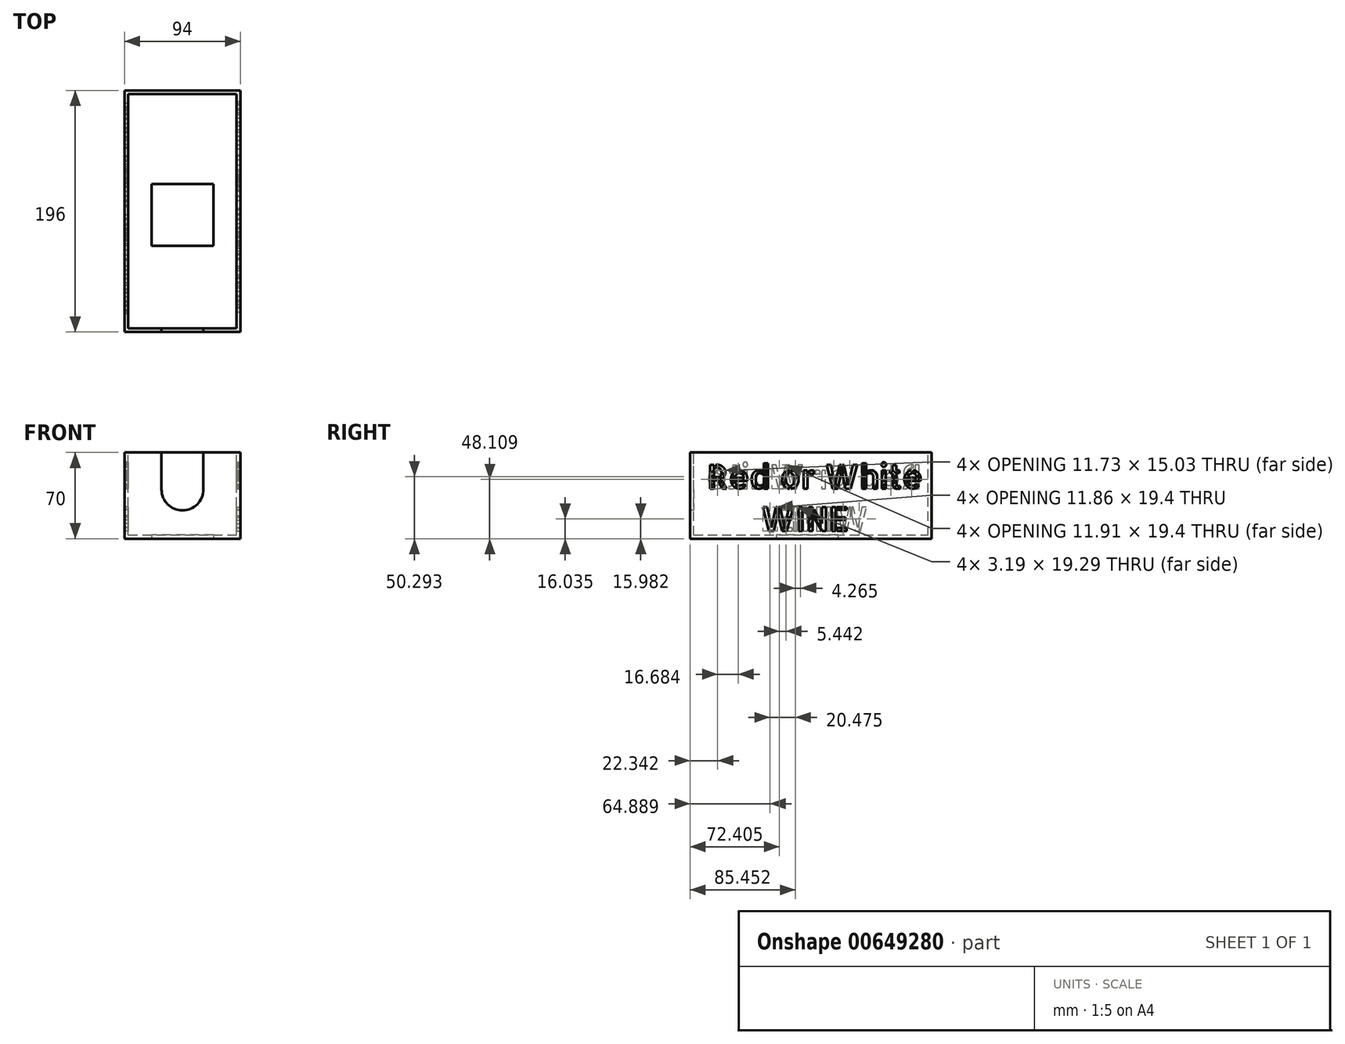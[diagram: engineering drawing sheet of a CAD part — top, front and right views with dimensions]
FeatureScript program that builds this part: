
annotation { "Feature Type Name" : "Feature", "Feature Type Description" : "" }
export const myFeature = defineFeature(function(context is Context, id is Id, definition is map)
    precondition{}
    {
        {
            var Q0;
            Q0=qCreatedBy(makeId("Front.planeOp"),FACE);
            var sketch = newSketch(context, id + "F0", { "sketchPlane" : qUnion([Q0])});
            skLineSegment(sketch, "E0.bottom", {"start": v(-47, 0) * mm, "end": v(47, 0) * mm});
            skLineSegment(sketch, "E0.top", {"start": v(-47, 70) * mm, "end": v(47, 70) * mm});
            skLineSegment(sketch, "E0.left", {"start": v(-47, 0) * mm, "end": v(-47, 70) * mm});
            skLineSegment(sketch, "E0.right", {"start": v(47, 0) * mm, "end": v(47, 70) * mm});
            skSolve(sketch);
        }
        {
            var Q0;
            Q0 = qSketchRegion(id + "F0", true);
            extrude(context, id + "F1", {"entities" : qUnion([Q0]), "depth" : 196 * mm, "offsetDistance" : 25 * mm});
        }
        {
            var Q0;
            Q0=makeQuery(id+"F1.opExtrude","SWEPT_FACE",FACE,{"disambiguationData":[OSD([sQuery(id+"F0.wireOp",EDGE,"E0.top")])]});
            shell(context, id + "F2", {"entities" : qUnion([Q0]), "thickness" : 3 * mm});
        }
        {
            var Q0;
            Q0=makeQuery(id+"F1.opExtrude","CAP_FACE",FACE,{"disambiguationData":[OSD([sQuery(id+"F0.wireOp",EDGE,"E0.bottom"),sQuery(id+"F0.wireOp",EDGE,"E0.top"),sQuery(id+"F0.wireOp",EDGE,"E0.left"),sQuery(id+"F0.wireOp",EDGE,"E0.right")])],"isStart":false});
            var sketch = newSketch(context, id + "F3", { "sketchPlane" : qUnion([Q0])});
            skArc(sketch, "E1", {"start": v(-17, 40) * mm, "mid": v(0, 23) * mm, "end": v(17, 40) * mm});
            skLineSegment(sketch, "E2", {"start": v(-17, 40) * mm, "end": v(-17, 70) * mm});
            skLineSegment(sketch, "E3", {"start": v(17, 40) * mm, "end": v(17, 70) * mm});
            skLineSegment(sketch, "E4", {"start": v(-17, 70) * mm, "end": v(17, 70) * mm});
            skSolve(sketch);
        }
        {
            var Q0;
            Q0 = qSketchRegion(id + "F3", true);
            extrude(context, id + "F4", {"entities" : qUnion([Q0]), "operationType" : NewBodyOperationType.REMOVE, "oppositeDirection" : true, "depth" : 25 * mm, "offsetDistance" : 25 * mm});
        }
        {
            var Q0;
            Q0=makeQuery(id+"F1.opExtrude","SWEPT_FACE",FACE,{"disambiguationData":[OSD([sQuery(id+"F0.wireOp",EDGE,"E0.right")])]});
            var sketch = newSketch(context, id + "F5", { "sketchPlane" : qUnion([Q0])});
            skText(sketch, "E5", { "text": "Red or White\n      WINE", "fontName": "AllertaStencil-Regular.ttf"});
            const initialGuessF5  = {"E5": [-0.182, 0.0407, 1, 0, 0.0193]};
            skSetInitialGuess(sketch, initialGuessF5);
            skSolve(sketch);
        }
        {
            var Q0;
            Q0 = qSketchRegion(id + "F5", true);
            extrude(context, id + "F6", {"entities" : qUnion([Q0]), "operationType" : NewBodyOperationType.REMOVE, "oppositeDirection" : true, "depth" : 25 * mm, "offsetDistance" : 25 * mm});
        }
        {
            var Q0;
            Q0=makeQuery(id+"F1.opExtrude","SWEPT_FACE",FACE,{"disambiguationData":[OSD([sQuery(id+"F0.wireOp",EDGE,"E0.left")])]});
            var sketch = newSketch(context, id + "F7", { "sketchPlane" : qUnion([Q0])});
            skText(sketch, "E6", { "text": "Red or White\n      WINE", "fontName": "AllertaStencil-Regular.ttf"});
            const initialGuessF7  = {"E6": [0.008, 0.0407, 1, 0, 0.0193]};
            skSetInitialGuess(sketch, initialGuessF7);
            skSolve(sketch);
        }
        {
            var Q0;
            Q0 = qSketchRegion(id + "F7", true);
            extrude(context, id + "F8", {"entities" : qUnion([Q0]), "operationType" : NewBodyOperationType.REMOVE, "oppositeDirection" : true, "depth" : 25 * mm, "offsetDistance" : 25 * mm});
        }
        {
            var Q0;
            Q0=makeQuery(id+"F1.opExtrude","SWEPT_FACE",FACE,{"disambiguationData":[OSD([sQuery(id+"F0.wireOp",EDGE,"E0.bottom")])]});
            var sketch = newSketch(context, id + "F9", { "sketchPlane" : qUnion([Q0])});
            skLineSegment(sketch, "E7.bottom", {"start": v(-25, 126) * mm, "end": v(25, 126) * mm});
            skLineSegment(sketch, "E7.top", {"start": v(-25, 76) * mm, "end": v(25, 76) * mm});
            skLineSegment(sketch, "E7.left", {"start": v(-25, 126) * mm, "end": v(-25, 76) * mm});
            skLineSegment(sketch, "E7.right", {"start": v(25, 126) * mm, "end": v(25, 76) * mm});
            skSolve(sketch);
        }
        {
            var Q0;
            Q0 = qSketchRegion(id + "F9", true);
            extrude(context, id + "F10", {"entities" : qUnion([Q0]), "operationType" : NewBodyOperationType.REMOVE, "oppositeDirection" : true, "depth" : 25 * mm, "offsetDistance" : 25 * mm});
        }
    });
